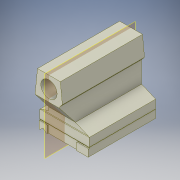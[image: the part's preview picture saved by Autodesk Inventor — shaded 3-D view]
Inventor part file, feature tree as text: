
AUTODESK INVENTOR PART (.ipt)
format: ipt  version: 2016 (Build 200138000, 138)  size: 402,432 bytes
history: native  units: mm
features: extrude x25, sketch x25, fillet x6, plane x2
ambient origin geometry x8: Origin, YZ Plane, XZ Plane, XY Plane, X Axis, Y Axis, Z Axis, Center Point
bodies: Solid1 (feature_tree)
feature tree (58):
  extrude  "Extrusion1"  Depth=151.0mm
  extrude  "Extrusion2"  Depth=25.0mm
  extrude  "Extrusion3"  Depth=4.0mm
  extrude  "Extrusion4"  Depth=10.0mm
  extrude  "Extrusion5"  Depth=25.0mm
  extrude  "Extrusion6"  Depth=2.0mm TaperAngle=0.0deg
  fillet  "Fillet1"  Radius=37.0mm
  extrude  "Extrusion7"  Depth=1.0mm TaperAngle=0.0deg
  fillet  "Fillet3"  Radius=5.0mm
  extrude  "Extrusion8"  Depth=5.0mm
  extrude  "Extrusion9"  Depth=1.0mm
  extrude  "Extrusion10"  Depth=1.0mm
  extrude  "Extrusion11"  Depth=1.0mm TaperAngle=0.0deg
  plane  "Work Plane1"
  extrude  "Extrusion12"  Depth=49.0mm TaperAngle=0.0deg
  extrude  "Extrusion13"  Depth=35.0mm
  extrude  "Extrusion14"  Depth=16.755161mm
  extrude  "Extrusion15"  Depth=295.5mm TaperAngle=0.0deg
  fillet  "Fillet4"  Radius=295.5mm
  extrude  "Extrusion16"  Depth=295.5mm TaperAngle=0.0deg
  extrude  "Extrusion17"  Depth=2.0mm
  plane  "Work Plane2"
  extrude  "Extrusion18"  Depth=50.0mm
  extrude  "Extrusion19"  Depth=5.0mm TaperAngle=0.0deg
  extrude  "Extrusion20"  Depth=1.0mm TaperAngle=0.0deg
  extrude  "Extrusion21"  Depth=207.0mm TaperAngle=0.0deg
  extrude  "Extrusion22"  Depth=204.0mm
  extrude  "Extrusion23"  Depth=6.981317mm
  extrude  "Extrusion24"  Depth=204.0mm TaperAngle=0.0deg
  fillet  "Fillet5"  Radius=25.3mm
  fillet  "Fillet6"  Radius=3.0mm
  extrude  "Extrusion25"  Depth=3.0mm
  fillet  "Fillet7"  Radius=36.2mm
  sketch  "Sketch1"  dims[d19=26.0mm d20=151.0mm]
  sketch  "Sketch2"  dims[d21=203.0mm d22=0.0mm d23=25.0mm]
  sketch  "Sketch3"  dims[d29=4.0mm d30=22.68928mm]
  sketch  "Sketch4"  dims[d31=8.726646mm d32=10.0mm]
  sketch  "Sketch5"  dims[d33=215.0mm d34=0.0mm d35=25.0mm]
  sketch  "Sketch6"  dims[d36=6.0mm d37=0.0mm d38=2.0mm d39=0.0mm d40=37.0mm]
  sketch  "Sketch8"  dims[d41=6.0mm d42=0.0mm d43=1.0mm d44=0.0mm d45=5.0mm]
  sketch  "Sketch9"  dims[d47=1.0mm d48=0.0mm d49=5.0mm]
  sketch  "Sketch10"  dims[d50=1.0mm d51=1.0mm]
  sketch  "Sketch11"  dims[d52=1.0mm d53=1.0mm]
  sketch  "Sketch12"  dims[d54=1.0mm d55=0.0mm d56=26.0mm d57=0.0mm]
  sketch  "Sketch13"  dims[d58=49.0mm d59=152.0mm d60=0.0mm]
  sketch  "Sketch14"  dims[d61=35.0mm d62=35.0mm]
  sketch  "Sketch15"  dims[d63=16.755161mm d64=16.755161mm]
  sketch  "Sketch16"  dims[d65=58.0mm d66=295.5mm d67=0.0mm d68=295.5mm d69=0.0mm]
  sketch  "Sketch18"  dims[d70=295.5mm d71=0.0mm d72=295.5mm d73=0.0mm]
  sketch  "Sketch19"  dims[d74=1.0mm d75=0.0mm d76=2.0mm]
  sketch  "Sketch20"  dims[d85=1.0mm d86=0.0mm d87=50.0mm]
  sketch  "Sketch21"  dims[d88=300.0mm d89=0.0mm d90=5.0mm d91=0.0mm]
  sketch  "Sketch23"  dims[d92=1.0mm d93=0.0mm d94=1.0mm d95=0.0mm]
  sketch  "Sketch24"  dims[d96=2.0mm d97=207.0mm d98=0.0mm]
  sketch  "Sketch25"  dims[d99=204.0mm d100=0.0mm d101=148.124mm]
  sketch  "Sketch26"  dims[d102=10.2mm d103=6.981317mm]
  sketch  "Sketch27"  dims[d104=3.8mm d106=204.0mm d107=0.0mm d108=25.3mm d109=3.0mm d110=0.0mm]
  sketch  "Sketch28"  dims[d111=3.0mm d112=3.0mm d113=36.2mm d114=3.0mm d115=0.0mm d116=3.0mm]
